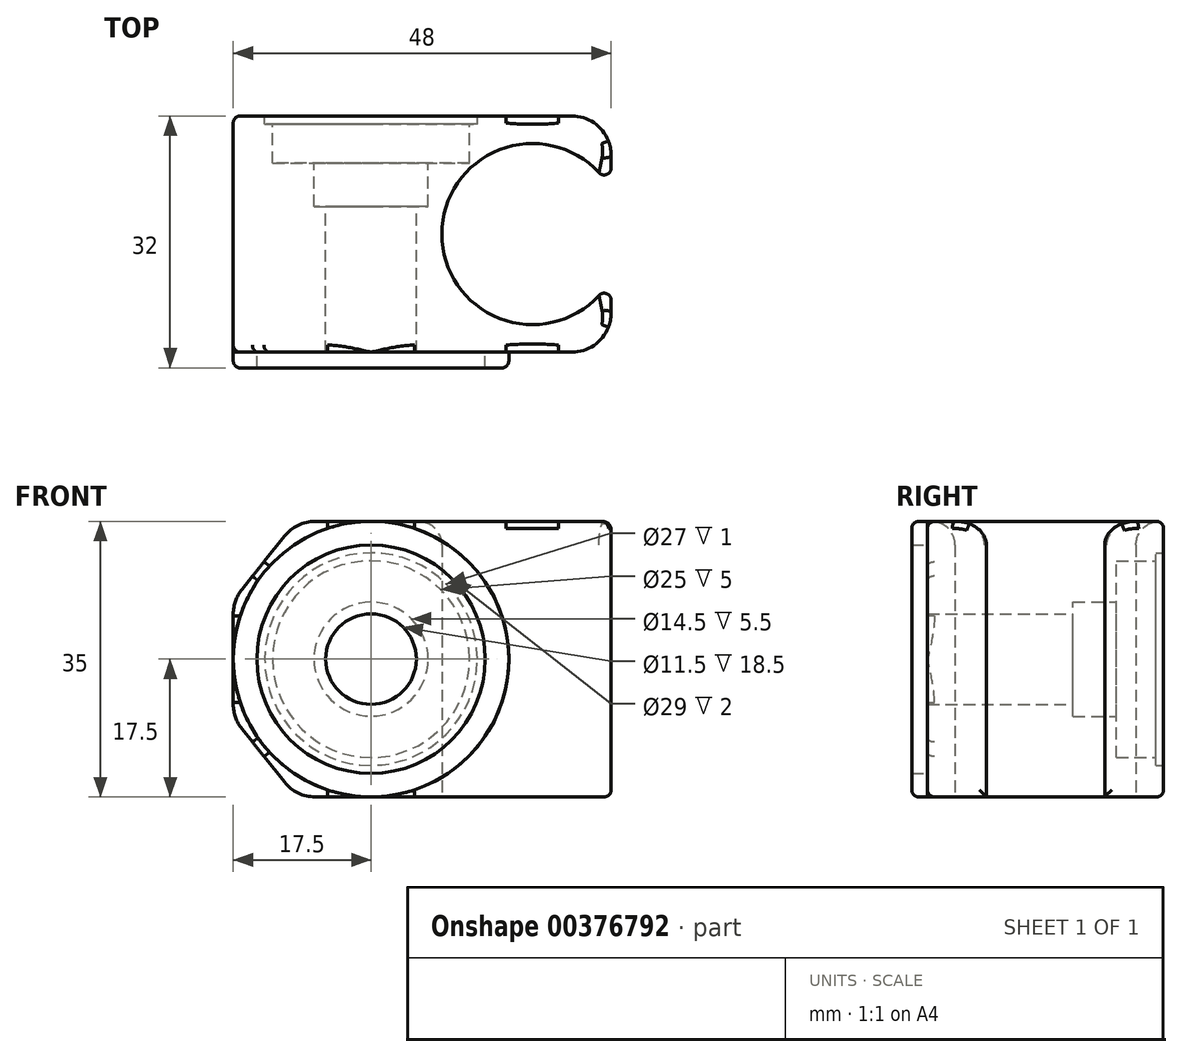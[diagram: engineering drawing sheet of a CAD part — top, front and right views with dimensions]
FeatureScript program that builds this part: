
annotation { "Feature Type Name" : "Feature", "Feature Type Description" : "" }
export const myFeature = defineFeature(function(context is Context, id is Id, definition is map)
    precondition{}
    {
        {
            var Q0;
            Q0=qCreatedBy(makeId("Front.planeOp"),FACE);
            var sketch = newSketch(context, id + "F0", { "sketchPlane" : qUnion([Q0])});
            skLineSegment(sketch, "E0.bottom", {"start": v(0, 0) * mm, "end": v(48, 0) * mm});
            skLineSegment(sketch, "E0.top", {"start": v(0, 35) * mm, "end": v(48, 35) * mm});
            skLineSegment(sketch, "E0.left", {"start": v(0, 0) * mm, "end": v(0, 35) * mm});
            skLineSegment(sketch, "E0.right", {"start": v(48, 0) * mm, "end": v(48, 35) * mm});
            skLineSegment(sketch, "E1", {"start": v(0, 17.5) * mm, "end": v(48, 17.5) * mm, "construction": true});
            skCircle(sketch, "E2", {"center": v(17.5, 17.5) * mm, "radius": 12.5 * mm});
            skCircle(sketch, "E3", {"center": v(17.5, 17.5) * mm, "radius": 7.25 * mm});
            skCircle(sketch, "E4", {"center": v(17.5, 17.5) * mm, "radius": 5.75 * mm});
            skCircle(sketch, "E5", {"center": v(17.5, 17.5) * mm, "radius": 13.5 * mm});
            skCircle(sketch, "E6", {"center": v(17.5, 17.5) * mm, "radius": 17.5 * mm});
            skCircle(sketch, "E7", {"center": v(17.5, 17.5) * mm, "radius": 14.5 * mm});
            skSolve(sketch);
        }
        {
            var Q0;
            {var subQ0=sQuery(id+"F0.wireOp",EDGE,"E0.left");var subQ1=sQuery(id+"F0.wireOp",EDGE,"E0.top");var subQ2=makeQuery(id+"F0.imprint","INTERSECT",VERTEX,{"derivedFrom":[subQ1,subQ0]});Q0=makeQuery(id+"F0.imprint","IMPRINT",FACE,{"disambiguationData":[TD([[makeQuery(id+"F0.imprint","IMPRINT",EDGE,{"disambiguationData":[TD([[subQ2,-1.0]])],"derivedFrom":subQ1}),-1.0]])]});}
            var Q1;
            {var subQ0=sQuery(id+"F0.wireOp",EDGE,"E0.right");Q1=makeQuery(id+"F0.imprint","IMPRINT",FACE,{"disambiguationData":[TD([[makeQuery(id+"F0.imprint","IMPRINT",EDGE,{"derivedFrom":subQ0}),1.0]])]});}
            var Q2;
            {var subQ0=sQuery(id+"F0.wireOp",EDGE,"E0.left");var subQ1=sQuery(id+"F0.wireOp",EDGE,"E0.bottom");var subQ2=makeQuery(id+"F0.imprint","INTERSECT",VERTEX,{"derivedFrom":[subQ1,subQ0]});Q2=makeQuery(id+"F0.imprint","IMPRINT",FACE,{"disambiguationData":[TD([[makeQuery(id+"F0.imprint","IMPRINT",EDGE,{"disambiguationData":[TD([[subQ2,-1.0]])],"derivedFrom":subQ1}),1.0]])]});}
            var Q3;
            Q3=makeQuery(id+"F0.imprint","IMPRINT",FACE,{"disambiguationData":[TD([[makeQuery(id+"F0.imprint","IMPRINT",EDGE,{"derivedFrom":sQuery(id+"F0.wireOp",EDGE,"E7")}),-1.0]])]});
            var Q4;
            Q4=makeQuery(id+"F0.imprint","IMPRINT",FACE,{"disambiguationData":[TD([[makeQuery(id+"F0.imprint","IMPRINT",EDGE,{"derivedFrom":sQuery(id+"F0.wireOp",EDGE,"E5")}),-1.0]])]});
            var Q5;
            Q5=makeQuery(id+"F0.imprint","IMPRINT",FACE,{"disambiguationData":[TD([[makeQuery(id+"F0.imprint","IMPRINT",EDGE,{"derivedFrom":sQuery(id+"F0.wireOp",EDGE,"E2")}),-1.0]])]});
            var Q6;
            Q6=makeQuery(id+"F0.imprint","IMPRINT",FACE,{"disambiguationData":[TD([[makeQuery(id+"F0.imprint","IMPRINT",EDGE,{"derivedFrom":sQuery(id+"F0.wireOp",EDGE,"E2")}),1.0]])]});
            var Q7;
            Q7=makeQuery(id+"F0.imprint","IMPRINT",FACE,{"disambiguationData":[TD([[makeQuery(id+"F0.imprint","IMPRINT",EDGE,{"derivedFrom":sQuery(id+"F0.wireOp",EDGE,"E3")}),1.0]])]});
            var Q8;
            Q8=makeQuery(id+"F0.imprint","IMPRINT",FACE,{"disambiguationData":[TD([[makeQuery(id+"F0.imprint","IMPRINT",EDGE,{"derivedFrom":sQuery(id+"F0.wireOp",EDGE,"E4")}),1.0]])]});
            extrude(context, id + "F1", {"entities" : qUnion([Q0, Q1, Q2, Q3, Q4, Q5, Q6, Q7, Q8]), "depth" : 30 * mm});
        }
        {
            var Q0;
            Q0=makeQuery(id+"F0.imprint","IMPRINT",FACE,{"disambiguationData":[TD([[makeQuery(id+"F0.imprint","IMPRINT",EDGE,{"derivedFrom":sQuery(id+"F0.wireOp",EDGE,"E2")}),-1.0]])]});
            var Q1;
            Q1=makeQuery(id+"F0.imprint","IMPRINT",FACE,{"disambiguationData":[TD([[makeQuery(id+"F0.imprint","IMPRINT",EDGE,{"derivedFrom":sQuery(id+"F0.wireOp",EDGE,"E2")}),1.0]])]});
            var Q2;
            Q2=makeQuery(id+"F0.imprint","IMPRINT",FACE,{"disambiguationData":[TD([[makeQuery(id+"F0.imprint","IMPRINT",EDGE,{"derivedFrom":sQuery(id+"F0.wireOp",EDGE,"E3")}),1.0]])]});
            var Q3;
            Q3=makeQuery(id+"F0.imprint","IMPRINT",FACE,{"disambiguationData":[TD([[makeQuery(id+"F0.imprint","IMPRINT",EDGE,{"derivedFrom":sQuery(id+"F0.wireOp",EDGE,"E4")}),1.0]])]});
            extrude(context, id + "F2", {"entities" : qUnion([Q0, Q1, Q2, Q3]), "operationType" : NewBodyOperationType.REMOVE, "depth" : 1 * mm});
        }
        {
            var Q0;
            Q0=makeQuery(id+"F0.imprint","IMPRINT",FACE,{"disambiguationData":[TD([[makeQuery(id+"F0.imprint","IMPRINT",EDGE,{"derivedFrom":sQuery(id+"F0.wireOp",EDGE,"E2")}),1.0]])]});
            var Q1;
            Q1=makeQuery(id+"F0.imprint","IMPRINT",FACE,{"disambiguationData":[TD([[makeQuery(id+"F0.imprint","IMPRINT",EDGE,{"derivedFrom":sQuery(id+"F0.wireOp",EDGE,"E4")}),1.0]])]});
            var Q2;
            Q2=makeQuery(id+"F0.imprint","IMPRINT",FACE,{"disambiguationData":[TD([[makeQuery(id+"F0.imprint","IMPRINT",EDGE,{"derivedFrom":sQuery(id+"F0.wireOp",EDGE,"E3")}),1.0]])]});
            extrude(context, id + "F3", {"entities" : qUnion([Q0, Q1, Q2]), "operationType" : NewBodyOperationType.REMOVE, "depth" : 6 * mm});
        }
        {
            var Q0;
            Q0=makeQuery(id+"F0.imprint","IMPRINT",FACE,{"disambiguationData":[TD([[makeQuery(id+"F0.imprint","IMPRINT",EDGE,{"derivedFrom":sQuery(id+"F0.wireOp",EDGE,"E3")}),1.0]])]});
            var Q1;
            Q1=makeQuery(id+"F0.imprint","IMPRINT",FACE,{"disambiguationData":[TD([[makeQuery(id+"F0.imprint","IMPRINT",EDGE,{"derivedFrom":sQuery(id+"F0.wireOp",EDGE,"E4")}),1.0]])]});
            extrude(context, id + "F4", {"entities" : qUnion([Q0, Q1]), "operationType" : NewBodyOperationType.REMOVE, "depth" : 11.5 * mm});
        }
        {
            var Q0;
            Q0=makeQuery(id+"F0.imprint","IMPRINT",FACE,{"disambiguationData":[TD([[makeQuery(id+"F0.imprint","IMPRINT",EDGE,{"derivedFrom":sQuery(id+"F0.wireOp",EDGE,"E4")}),1.0]])]});
            extrude(context, id + "F5", {"entities" : qUnion([Q0]), "operationType" : NewBodyOperationType.REMOVE, "endBound" : BoundingType.THROUGH_ALL, "depth" : 25 * mm});
        }
        {
            var Q0;
            Q0=makeQuery(id+"F0.imprint","IMPRINT",FACE,{"disambiguationData":[TD([[makeQuery(id+"F0.imprint","IMPRINT",EDGE,{"derivedFrom":sQuery(id+"F0.wireOp",EDGE,"E7")}),-1.0]])]});
            extrude(context, id + "F6", {"entities" : qUnion([Q0]), "operationType" : NewBodyOperationType.ADD, "depth" : 32 * mm});
        }
        {
            var Q0;
            Q0=qCreatedBy(makeId("Top.planeOp"),FACE);
            var sketch = newSketch(context, id + "F7", { "sketchPlane" : qUnion([Q0])});
            skCircle(sketch, "E8", {"center": v(38, -15) * mm, "radius": 11.5 * mm});
            skLineSegment(sketch, "E9", {"start": v(48, -15) * mm, "end": v(0, -15) * mm, "construction": true});
            skSolve(sketch);
        }
        {
            var Q0;
            Q0=makeQuery(id+"F7.imprint","IMPRINT",FACE,{"disambiguationData":[TD([[makeQuery(id+"F7.imprint","IMPRINT",EDGE,{"derivedFrom":sQuery(id+"F7.wireOp",EDGE,"E8")}),1.0]])]});
            extrude(context, id + "F8", {"entities" : qUnion([Q0]), "operationType" : NewBodyOperationType.REMOVE, "endBound" : BoundingType.THROUGH_ALL, "depth" : 25 * mm});
        }
        {
            var Q0;
            Q0=makeQuery(id+"F1.opExtrude","SWEPT_EDGE",EDGE,{"disambiguationData":[OSD([sQuery(id+"F0.wireOp",EDGE,"E0.bottom"),sQuery(id+"F0.wireOp",EDGE,"E0.left")])]});
            var Q1;
            Q1=makeQuery(id+"F1.opExtrude","SWEPT_EDGE",EDGE,{"disambiguationData":[OSD([sQuery(id+"F0.wireOp",EDGE,"E0.top"),sQuery(id+"F0.wireOp",EDGE,"E0.left")])]});
            chamfer(context, id + "F9", {"entities" : qUnion([Q0, Q1]), "chamferType" : ChamferType.TWO_OFFSETS, "width1" : 8 * mm, "oppositeDirection" : false, "width2" : 10 * mm, "tangentPropagation" : true});
        }
        {
            var Q0;
            {var subQ0=sQuery(id+"F0.wireOp",EDGE,"E0.left");Q0=makeQuery(id+"F9.opChamfer","BLEND_EDGE",EDGE,{"blendedFrom":[makeQuery(id+"F1.opExtrude","SWEPT_EDGE",EDGE,{"disambiguationData":[OSD([sQuery(id+"F0.wireOp",EDGE,"E0.bottom"),subQ0])]}),makeQuery(id+"F1.opExtrude","SWEPT_FACE",FACE,{"disambiguationData":[OSD([subQ0])]})],"blendedInto":[makeQuery(id+"F1.opExtrude","SWEPT_FACE",FACE,{"disambiguationData":[OSD([subQ0])]})]});}
            var Q1;
            {var subQ0=sQuery(id+"F0.wireOp",EDGE,"E0.left");Q1=makeQuery(id+"F9.opChamfer","BLEND_EDGE",EDGE,{"blendedFrom":[makeQuery(id+"F1.opExtrude","SWEPT_EDGE",EDGE,{"disambiguationData":[OSD([sQuery(id+"F0.wireOp",EDGE,"E0.top"),subQ0])]}),makeQuery(id+"F1.opExtrude","SWEPT_FACE",FACE,{"disambiguationData":[OSD([subQ0])]})],"blendedInto":[makeQuery(id+"F1.opExtrude","SWEPT_FACE",FACE,{"disambiguationData":[OSD([subQ0])]})]});}
            var Q2;
            {var subQ0=sQuery(id+"F0.wireOp",EDGE,"E0.top");Q2=makeQuery(id+"F9.opChamfer","BLEND_EDGE",EDGE,{"blendedFrom":[makeQuery(id+"F1.opExtrude","SWEPT_EDGE",EDGE,{"disambiguationData":[OSD([subQ0,sQuery(id+"F0.wireOp",EDGE,"E0.left")])]}),makeQuery(id+"F1.opExtrude","SWEPT_FACE",FACE,{"disambiguationData":[OSD([subQ0])]})],"blendedInto":[makeQuery(id+"F1.opExtrude","SWEPT_FACE",FACE,{"disambiguationData":[OSD([subQ0])]})]});}
            var Q3;
            {var subQ0=sQuery(id+"F0.wireOp",EDGE,"E0.bottom");Q3=makeQuery(id+"F9.opChamfer","BLEND_EDGE",EDGE,{"blendedFrom":[makeQuery(id+"F1.opExtrude","SWEPT_EDGE",EDGE,{"disambiguationData":[OSD([subQ0,sQuery(id+"F0.wireOp",EDGE,"E0.left")])]}),makeQuery(id+"F1.opExtrude","SWEPT_FACE",FACE,{"disambiguationData":[OSD([subQ0])]})],"blendedInto":[makeQuery(id+"F1.opExtrude","SWEPT_FACE",FACE,{"disambiguationData":[OSD([subQ0])]})]});}
            var Q4;
            Q4=makeQuery(id+"F1.opExtrude","CAP_EDGE",EDGE,{"disambiguationData":[OSD([sQuery(id+"F0.wireOp",EDGE,"E0.right")])],"isStart":false});
            var Q5;
            Q5=makeQuery(id+"F1.opExtrude","CAP_EDGE",EDGE,{"disambiguationData":[OSD([sQuery(id+"F0.wireOp",EDGE,"E0.right")])],"isStart":true});
            fillet(context, id + "F10", {"entities" : qUnion([Q0, Q1, Q2, Q3, Q4, Q5]), "radius" : 5 * mm, "tangentPropagation" : true, "allowEdgeOverflow" : false});
        }
        {
            var Q0;
            Q0=makeQuery(id+"F8.boolean.opBoolean","INTERSECT",EDGE,{"derivedFrom":[makeQuery(id+"F1.opExtrude","SWEPT_FACE",FACE,{"disambiguationData":[OSD([sQuery(id+"F0.wireOp",EDGE,"E0.top")])]}),makeQuery(id+"F8.opExtrude","SWEPT_FACE",FACE,{"disambiguationData":[OSD([sQuery(id+"F7.wireOp",EDGE,"E8")])]})]});
            var Q1;
            Q1=makeQuery(id+"F8.boolean.opBoolean","COPY",EDGE,{"derivedFrom":makeQuery(id+"F8.opExtrude","CAP_EDGE",EDGE,{"disambiguationData":[OSD([sQuery(id+"F7.wireOp",EDGE,"E8")])],"isStart":true})});
            fillet(context, id + "F11", {"entities" : qUnion([Q0, Q1]), "radius" : 3 * mm, "tangentPropagation" : true, "allowEdgeOverflow" : false});
        }
        {
            var Q0;
            {var subQ0=sQuery(id+"F0.wireOp",EDGE,"E0.bottom");var subQ1=sQuery(id+"F0.wireOp",EDGE,"E0.right");Q0=makeQuery(id+"F6.boolean.opBoolean","SPLIT",EDGE,{"disambiguationData":[TD([makeQuery(id+"F1.opExtrude","SWEPT_FACE",FACE,{"disambiguationData":[OSD([subQ1])]})])],"derivedFrom":makeQuery(id+"F1.opExtrude","CAP_EDGE",EDGE,{"disambiguationData":[OSD([subQ0])],"isStart":false})});}
            var Q1;
            Q1=makeQuery(id+"F10.opFillet","BLEND_EDGE",EDGE,{"blendedFrom":[makeQuery(id+"F1.opExtrude","CAP_EDGE",EDGE,{"disambiguationData":[OSD([sQuery(id+"F0.wireOp",EDGE,"E0.right")])],"isStart":false}),makeQuery(id+"F1.opExtrude","SWEPT_FACE",FACE,{"disambiguationData":[OSD([sQuery(id+"F0.wireOp",EDGE,"E0.bottom")])]})],"blendedInto":[makeQuery(id+"F1.opExtrude","SWEPT_FACE",FACE,{"disambiguationData":[OSD([sQuery(id+"F0.wireOp",EDGE,"E0.bottom")])]})]});
            var Q2;
            {var subQ0=sQuery(id+"F0.wireOp",EDGE,"E0.bottom");var subQ1=sQuery(id+"F0.wireOp",EDGE,"E0.left");Q2=makeQuery(id+"F6.boolean.opBoolean","SPLIT",EDGE,{"disambiguationData":[TD([makeQuery(id+"F1.opExtrude","SWEPT_FACE",FACE,{"disambiguationData":[OSD([subQ1])]})])],"derivedFrom":makeQuery(id+"F1.opExtrude","CAP_EDGE",EDGE,{"disambiguationData":[OSD([subQ0])],"isStart":false})});}
            var Q3;
            {var subQ0=sQuery(id+"F0.wireOp",EDGE,"E0.bottom");var subQ1=makeQuery(id+"F1.opExtrude","SWEPT_FACE",FACE,{"disambiguationData":[OSD([subQ0])]});var subQ2=sQuery(id+"F0.wireOp",EDGE,"E0.left");var subQ3=makeQuery(id+"F1.opExtrude","CAP_FACE",FACE,{"disambiguationData":[OSD([subQ0,sQuery(id+"F0.wireOp",EDGE,"E0.top"),subQ2,sQuery(id+"F0.wireOp",EDGE,"E0.right")])],"isStart":false});Q3=makeQuery(id+"F10.opFillet","BLEND_EDGE",EDGE,{"blendedFrom":[makeQuery(id+"F9.opChamfer","BLEND_EDGE",EDGE,{"blendedFrom":[makeQuery(id+"F1.opExtrude","SWEPT_EDGE",EDGE,{"disambiguationData":[OSD([subQ0,subQ2])]}),subQ1],"blendedInto":[subQ1]}),makeQuery(id+"F6.boolean.opBoolean","SPLIT",FACE,{"disambiguationData":[TD([subQ1,subQ3,makeQuery(id+"F1.opExtrude","SWEPT_FACE",FACE,{"disambiguationData":[OSD([subQ2])]}),makeQuery(id+"F6.opExtrude","SWEPT_FACE",FACE,{"disambiguationData":[OSD([sQuery(id+"F0.wireOp",EDGE,"E6")])]})])],"derivedFrom":subQ3})],"blendedInto":[makeQuery(id+"F6.boolean.opBoolean","SPLIT",FACE,{"disambiguationData":[TD([subQ1,subQ3,makeQuery(id+"F1.opExtrude","SWEPT_FACE",FACE,{"disambiguationData":[OSD([subQ2])]}),makeQuery(id+"F6.opExtrude","SWEPT_FACE",FACE,{"disambiguationData":[OSD([sQuery(id+"F0.wireOp",EDGE,"E6")])]})])],"derivedFrom":subQ3})]});}
            var Q4;
            {var subQ0=sQuery(id+"F0.wireOp",EDGE,"E0.bottom");var subQ1=sQuery(id+"F0.wireOp",EDGE,"E0.left");var subQ2=makeQuery(id+"F1.opExtrude","CAP_FACE",FACE,{"disambiguationData":[OSD([subQ0,sQuery(id+"F0.wireOp",EDGE,"E0.top"),subQ1,sQuery(id+"F0.wireOp",EDGE,"E0.right")])],"isStart":false});Q4=makeQuery(id+"F9.opChamfer","BLEND_EDGE",EDGE,{"blendedFrom":[makeQuery(id+"F1.opExtrude","SWEPT_EDGE",EDGE,{"disambiguationData":[OSD([subQ0,subQ1])]}),makeQuery(id+"F6.boolean.opBoolean","SPLIT",FACE,{"disambiguationData":[TD([makeQuery(id+"F1.opExtrude","SWEPT_FACE",FACE,{"disambiguationData":[OSD([subQ0])]}),subQ2,makeQuery(id+"F1.opExtrude","SWEPT_FACE",FACE,{"disambiguationData":[OSD([subQ1])]}),makeQuery(id+"F6.opExtrude","SWEPT_FACE",FACE,{"disambiguationData":[OSD([sQuery(id+"F0.wireOp",EDGE,"E6")])]})])],"derivedFrom":subQ2})],"blendedInto":[makeQuery(id+"F6.boolean.opBoolean","SPLIT",FACE,{"disambiguationData":[TD([makeQuery(id+"F1.opExtrude","SWEPT_FACE",FACE,{"disambiguationData":[OSD([subQ0])]}),subQ2,makeQuery(id+"F1.opExtrude","SWEPT_FACE",FACE,{"disambiguationData":[OSD([subQ1])]}),makeQuery(id+"F6.opExtrude","SWEPT_FACE",FACE,{"disambiguationData":[OSD([sQuery(id+"F0.wireOp",EDGE,"E6")])]})])],"derivedFrom":subQ2})]});}
            var Q5;
            {var subQ0=sQuery(id+"F0.wireOp",EDGE,"E0.bottom");var subQ1=sQuery(id+"F0.wireOp",EDGE,"E0.left");var subQ2=makeQuery(id+"F1.opExtrude","CAP_FACE",FACE,{"disambiguationData":[OSD([subQ0,sQuery(id+"F0.wireOp",EDGE,"E0.top"),subQ1,sQuery(id+"F0.wireOp",EDGE,"E0.right")])],"isStart":false});var subQ3=makeQuery(id+"F1.opExtrude","SWEPT_FACE",FACE,{"disambiguationData":[OSD([subQ1])]});Q5=makeQuery(id+"F10.opFillet","BLEND_EDGE",EDGE,{"blendedFrom":[makeQuery(id+"F9.opChamfer","BLEND_EDGE",EDGE,{"blendedFrom":[makeQuery(id+"F1.opExtrude","SWEPT_EDGE",EDGE,{"disambiguationData":[OSD([subQ0,subQ1])]}),subQ3],"blendedInto":[subQ3]}),makeQuery(id+"F6.boolean.opBoolean","SPLIT",FACE,{"disambiguationData":[TD([makeQuery(id+"F1.opExtrude","SWEPT_FACE",FACE,{"disambiguationData":[OSD([subQ0])]}),subQ2,subQ3,makeQuery(id+"F6.opExtrude","SWEPT_FACE",FACE,{"disambiguationData":[OSD([sQuery(id+"F0.wireOp",EDGE,"E6")])]})])],"derivedFrom":subQ2})],"blendedInto":[makeQuery(id+"F6.boolean.opBoolean","SPLIT",FACE,{"disambiguationData":[TD([makeQuery(id+"F1.opExtrude","SWEPT_FACE",FACE,{"disambiguationData":[OSD([subQ0])]}),subQ2,subQ3,makeQuery(id+"F6.opExtrude","SWEPT_FACE",FACE,{"disambiguationData":[OSD([sQuery(id+"F0.wireOp",EDGE,"E6")])]})])],"derivedFrom":subQ2})]});}
            var Q6;
            {var subQ0=sQuery(id+"F0.wireOp",EDGE,"E0.bottom");var subQ1=sQuery(id+"F0.wireOp",EDGE,"E0.left");Q6=makeQuery(id+"F6.boolean.opBoolean","SPLIT",EDGE,{"disambiguationData":[TD([makeQuery(id+"F1.opExtrude","SWEPT_FACE",FACE,{"disambiguationData":[OSD([subQ0])]})])],"derivedFrom":makeQuery(id+"F1.opExtrude","CAP_EDGE",EDGE,{"disambiguationData":[OSD([subQ1])],"isStart":false})});}
            var Q7;
            {var subQ0=sQuery(id+"F0.wireOp",EDGE,"E0.left");var subQ1=sQuery(id+"F0.wireOp",EDGE,"E0.top");Q7=makeQuery(id+"F6.boolean.opBoolean","SPLIT",EDGE,{"disambiguationData":[TD([makeQuery(id+"F1.opExtrude","SWEPT_FACE",FACE,{"disambiguationData":[OSD([subQ1])]})])],"derivedFrom":makeQuery(id+"F1.opExtrude","CAP_EDGE",EDGE,{"disambiguationData":[OSD([subQ0])],"isStart":false})});}
            var Q8;
            {var subQ0=sQuery(id+"F0.wireOp",EDGE,"E0.left");var subQ1=sQuery(id+"F0.wireOp",EDGE,"E0.top");var subQ2=makeQuery(id+"F1.opExtrude","CAP_FACE",FACE,{"disambiguationData":[OSD([sQuery(id+"F0.wireOp",EDGE,"E0.bottom"),subQ1,subQ0,sQuery(id+"F0.wireOp",EDGE,"E0.right")])],"isStart":false});var subQ3=makeQuery(id+"F1.opExtrude","SWEPT_FACE",FACE,{"disambiguationData":[OSD([subQ0])]});Q8=makeQuery(id+"F10.opFillet","BLEND_EDGE",EDGE,{"blendedFrom":[makeQuery(id+"F9.opChamfer","BLEND_EDGE",EDGE,{"blendedFrom":[makeQuery(id+"F1.opExtrude","SWEPT_EDGE",EDGE,{"disambiguationData":[OSD([subQ1,subQ0])]}),subQ3],"blendedInto":[subQ3]}),makeQuery(id+"F6.boolean.opBoolean","SPLIT",FACE,{"disambiguationData":[TD([subQ2,makeQuery(id+"F1.opExtrude","SWEPT_FACE",FACE,{"disambiguationData":[OSD([subQ1])]}),subQ3,makeQuery(id+"F6.opExtrude","SWEPT_FACE",FACE,{"disambiguationData":[OSD([sQuery(id+"F0.wireOp",EDGE,"E6")])]})])],"derivedFrom":subQ2})],"blendedInto":[makeQuery(id+"F6.boolean.opBoolean","SPLIT",FACE,{"disambiguationData":[TD([subQ2,makeQuery(id+"F1.opExtrude","SWEPT_FACE",FACE,{"disambiguationData":[OSD([subQ1])]}),subQ3,makeQuery(id+"F6.opExtrude","SWEPT_FACE",FACE,{"disambiguationData":[OSD([sQuery(id+"F0.wireOp",EDGE,"E6")])]})])],"derivedFrom":subQ2})]});}
            var Q9;
            {var subQ0=sQuery(id+"F0.wireOp",EDGE,"E0.left");var subQ1=sQuery(id+"F0.wireOp",EDGE,"E0.top");var subQ2=makeQuery(id+"F1.opExtrude","CAP_FACE",FACE,{"disambiguationData":[OSD([sQuery(id+"F0.wireOp",EDGE,"E0.bottom"),subQ1,subQ0,sQuery(id+"F0.wireOp",EDGE,"E0.right")])],"isStart":false});Q9=makeQuery(id+"F9.opChamfer","BLEND_EDGE",EDGE,{"blendedFrom":[makeQuery(id+"F1.opExtrude","SWEPT_EDGE",EDGE,{"disambiguationData":[OSD([subQ1,subQ0])]}),makeQuery(id+"F6.boolean.opBoolean","SPLIT",FACE,{"disambiguationData":[TD([subQ2,makeQuery(id+"F1.opExtrude","SWEPT_FACE",FACE,{"disambiguationData":[OSD([subQ1])]}),makeQuery(id+"F1.opExtrude","SWEPT_FACE",FACE,{"disambiguationData":[OSD([subQ0])]}),makeQuery(id+"F6.opExtrude","SWEPT_FACE",FACE,{"disambiguationData":[OSD([sQuery(id+"F0.wireOp",EDGE,"E6")])]})])],"derivedFrom":subQ2})],"blendedInto":[makeQuery(id+"F6.boolean.opBoolean","SPLIT",FACE,{"disambiguationData":[TD([subQ2,makeQuery(id+"F1.opExtrude","SWEPT_FACE",FACE,{"disambiguationData":[OSD([subQ1])]}),makeQuery(id+"F1.opExtrude","SWEPT_FACE",FACE,{"disambiguationData":[OSD([subQ0])]}),makeQuery(id+"F6.opExtrude","SWEPT_FACE",FACE,{"disambiguationData":[OSD([sQuery(id+"F0.wireOp",EDGE,"E6")])]})])],"derivedFrom":subQ2})]});}
            var Q10;
            {var subQ0=sQuery(id+"F0.wireOp",EDGE,"E0.left");var subQ1=sQuery(id+"F0.wireOp",EDGE,"E0.top");Q10=makeQuery(id+"F6.boolean.opBoolean","SPLIT",EDGE,{"disambiguationData":[TD([makeQuery(id+"F1.opExtrude","SWEPT_FACE",FACE,{"disambiguationData":[OSD([subQ0])]})])],"derivedFrom":makeQuery(id+"F1.opExtrude","CAP_EDGE",EDGE,{"disambiguationData":[OSD([subQ1])],"isStart":false})});}
            var Q11;
            {var subQ0=sQuery(id+"F0.wireOp",EDGE,"E0.right");var subQ1=sQuery(id+"F0.wireOp",EDGE,"E0.top");Q11=makeQuery(id+"F6.boolean.opBoolean","SPLIT",EDGE,{"disambiguationData":[TD([makeQuery(id+"F1.opExtrude","SWEPT_FACE",FACE,{"disambiguationData":[OSD([subQ0])]})])],"derivedFrom":makeQuery(id+"F1.opExtrude","CAP_EDGE",EDGE,{"disambiguationData":[OSD([subQ1])],"isStart":false})});}
            var Q12;
            Q12=makeQuery(id+"F10.opFillet","BLEND_EDGE",EDGE,{"blendedFrom":[makeQuery(id+"F1.opExtrude","CAP_EDGE",EDGE,{"disambiguationData":[OSD([sQuery(id+"F0.wireOp",EDGE,"E0.right")])],"isStart":false}),makeQuery(id+"F1.opExtrude","SWEPT_FACE",FACE,{"disambiguationData":[OSD([sQuery(id+"F0.wireOp",EDGE,"E0.top")])]})],"blendedInto":[makeQuery(id+"F1.opExtrude","SWEPT_FACE",FACE,{"disambiguationData":[OSD([sQuery(id+"F0.wireOp",EDGE,"E0.top")])]})]});
            var Q13;
            Q13=makeQuery(id+"F1.opExtrude","CAP_EDGE",EDGE,{"disambiguationData":[OSD([sQuery(id+"F0.wireOp",EDGE,"E0.top")])],"isStart":true});
            var Q14;
            Q14=makeQuery(id+"F10.opFillet","BLEND_EDGE",EDGE,{"blendedFrom":[makeQuery(id+"F1.opExtrude","CAP_EDGE",EDGE,{"disambiguationData":[OSD([sQuery(id+"F0.wireOp",EDGE,"E0.right")])],"isStart":true}),makeQuery(id+"F1.opExtrude","SWEPT_FACE",FACE,{"disambiguationData":[OSD([sQuery(id+"F0.wireOp",EDGE,"E0.top")])]})],"blendedInto":[makeQuery(id+"F1.opExtrude","SWEPT_FACE",FACE,{"disambiguationData":[OSD([sQuery(id+"F0.wireOp",EDGE,"E0.top")])]})]});
            var Q15;
            {var subQ0=sQuery(id+"F0.wireOp",EDGE,"E0.left");var subQ1=sQuery(id+"F0.wireOp",EDGE,"E0.top");Q15=makeQuery(id+"F10.opFillet","BLEND_EDGE",EDGE,{"blendedFrom":[makeQuery(id+"F9.opChamfer","BLEND_EDGE",EDGE,{"blendedFrom":[makeQuery(id+"F1.opExtrude","SWEPT_EDGE",EDGE,{"disambiguationData":[OSD([subQ1,subQ0])]}),makeQuery(id+"F1.opExtrude","SWEPT_FACE",FACE,{"disambiguationData":[OSD([subQ1])]})],"blendedInto":[makeQuery(id+"F1.opExtrude","SWEPT_FACE",FACE,{"disambiguationData":[OSD([subQ1])]})]}),makeQuery(id+"F1.opExtrude","CAP_FACE",FACE,{"disambiguationData":[OSD([sQuery(id+"F0.wireOp",EDGE,"E0.bottom"),subQ1,subQ0,sQuery(id+"F0.wireOp",EDGE,"E0.right")])],"isStart":true})],"blendedInto":[makeQuery(id+"F1.opExtrude","CAP_FACE",FACE,{"disambiguationData":[OSD([sQuery(id+"F0.wireOp",EDGE,"E0.bottom"),subQ1,subQ0,sQuery(id+"F0.wireOp",EDGE,"E0.right")])],"isStart":true})]});}
            var Q16;
            {var subQ0=sQuery(id+"F0.wireOp",EDGE,"E0.left");var subQ1=sQuery(id+"F0.wireOp",EDGE,"E0.top");Q16=makeQuery(id+"F9.opChamfer","BLEND_EDGE",EDGE,{"blendedFrom":[makeQuery(id+"F1.opExtrude","SWEPT_EDGE",EDGE,{"disambiguationData":[OSD([subQ1,subQ0])]}),makeQuery(id+"F1.opExtrude","CAP_FACE",FACE,{"disambiguationData":[OSD([sQuery(id+"F0.wireOp",EDGE,"E0.bottom"),subQ1,subQ0,sQuery(id+"F0.wireOp",EDGE,"E0.right")])],"isStart":true})],"blendedInto":[makeQuery(id+"F1.opExtrude","CAP_FACE",FACE,{"disambiguationData":[OSD([sQuery(id+"F0.wireOp",EDGE,"E0.bottom"),subQ1,subQ0,sQuery(id+"F0.wireOp",EDGE,"E0.right")])],"isStart":true})]});}
            var Q17;
            {var subQ0=sQuery(id+"F0.wireOp",EDGE,"E0.left");var subQ1=sQuery(id+"F0.wireOp",EDGE,"E0.top");Q17=makeQuery(id+"F10.opFillet","BLEND_EDGE",EDGE,{"blendedFrom":[makeQuery(id+"F9.opChamfer","BLEND_EDGE",EDGE,{"blendedFrom":[makeQuery(id+"F1.opExtrude","SWEPT_EDGE",EDGE,{"disambiguationData":[OSD([subQ1,subQ0])]}),makeQuery(id+"F1.opExtrude","SWEPT_FACE",FACE,{"disambiguationData":[OSD([subQ0])]})],"blendedInto":[makeQuery(id+"F1.opExtrude","SWEPT_FACE",FACE,{"disambiguationData":[OSD([subQ0])]})]}),makeQuery(id+"F1.opExtrude","CAP_FACE",FACE,{"disambiguationData":[OSD([sQuery(id+"F0.wireOp",EDGE,"E0.bottom"),subQ1,subQ0,sQuery(id+"F0.wireOp",EDGE,"E0.right")])],"isStart":true})],"blendedInto":[makeQuery(id+"F1.opExtrude","CAP_FACE",FACE,{"disambiguationData":[OSD([sQuery(id+"F0.wireOp",EDGE,"E0.bottom"),subQ1,subQ0,sQuery(id+"F0.wireOp",EDGE,"E0.right")])],"isStart":true})]});}
            var Q18;
            Q18=makeQuery(id+"F1.opExtrude","CAP_EDGE",EDGE,{"disambiguationData":[OSD([sQuery(id+"F0.wireOp",EDGE,"E0.left")])],"isStart":true});
            var Q19;
            {var subQ0=sQuery(id+"F0.wireOp",EDGE,"E0.left");var subQ1=sQuery(id+"F0.wireOp",EDGE,"E0.bottom");Q19=makeQuery(id+"F10.opFillet","BLEND_EDGE",EDGE,{"blendedFrom":[makeQuery(id+"F9.opChamfer","BLEND_EDGE",EDGE,{"blendedFrom":[makeQuery(id+"F1.opExtrude","SWEPT_EDGE",EDGE,{"disambiguationData":[OSD([subQ1,subQ0])]}),makeQuery(id+"F1.opExtrude","SWEPT_FACE",FACE,{"disambiguationData":[OSD([subQ0])]})],"blendedInto":[makeQuery(id+"F1.opExtrude","SWEPT_FACE",FACE,{"disambiguationData":[OSD([subQ0])]})]}),makeQuery(id+"F1.opExtrude","CAP_FACE",FACE,{"disambiguationData":[OSD([subQ1,sQuery(id+"F0.wireOp",EDGE,"E0.top"),subQ0,sQuery(id+"F0.wireOp",EDGE,"E0.right")])],"isStart":true})],"blendedInto":[makeQuery(id+"F1.opExtrude","CAP_FACE",FACE,{"disambiguationData":[OSD([subQ1,sQuery(id+"F0.wireOp",EDGE,"E0.top"),subQ0,sQuery(id+"F0.wireOp",EDGE,"E0.right")])],"isStart":true})]});}
            var Q20;
            {var subQ0=sQuery(id+"F0.wireOp",EDGE,"E0.left");var subQ1=sQuery(id+"F0.wireOp",EDGE,"E0.bottom");Q20=makeQuery(id+"F9.opChamfer","BLEND_EDGE",EDGE,{"blendedFrom":[makeQuery(id+"F1.opExtrude","SWEPT_EDGE",EDGE,{"disambiguationData":[OSD([subQ1,subQ0])]}),makeQuery(id+"F1.opExtrude","CAP_FACE",FACE,{"disambiguationData":[OSD([subQ1,sQuery(id+"F0.wireOp",EDGE,"E0.top"),subQ0,sQuery(id+"F0.wireOp",EDGE,"E0.right")])],"isStart":true})],"blendedInto":[makeQuery(id+"F1.opExtrude","CAP_FACE",FACE,{"disambiguationData":[OSD([subQ1,sQuery(id+"F0.wireOp",EDGE,"E0.top"),subQ0,sQuery(id+"F0.wireOp",EDGE,"E0.right")])],"isStart":true})]});}
            var Q21;
            {var subQ0=sQuery(id+"F0.wireOp",EDGE,"E0.left");var subQ1=sQuery(id+"F0.wireOp",EDGE,"E0.bottom");Q21=makeQuery(id+"F10.opFillet","BLEND_EDGE",EDGE,{"blendedFrom":[makeQuery(id+"F9.opChamfer","BLEND_EDGE",EDGE,{"blendedFrom":[makeQuery(id+"F1.opExtrude","SWEPT_EDGE",EDGE,{"disambiguationData":[OSD([subQ1,subQ0])]}),makeQuery(id+"F1.opExtrude","SWEPT_FACE",FACE,{"disambiguationData":[OSD([subQ1])]})],"blendedInto":[makeQuery(id+"F1.opExtrude","SWEPT_FACE",FACE,{"disambiguationData":[OSD([subQ1])]})]}),makeQuery(id+"F1.opExtrude","CAP_FACE",FACE,{"disambiguationData":[OSD([subQ1,sQuery(id+"F0.wireOp",EDGE,"E0.top"),subQ0,sQuery(id+"F0.wireOp",EDGE,"E0.right")])],"isStart":true})],"blendedInto":[makeQuery(id+"F1.opExtrude","CAP_FACE",FACE,{"disambiguationData":[OSD([subQ1,sQuery(id+"F0.wireOp",EDGE,"E0.top"),subQ0,sQuery(id+"F0.wireOp",EDGE,"E0.right")])],"isStart":true})]});}
            var Q22;
            Q22=makeQuery(id+"F1.opExtrude","CAP_EDGE",EDGE,{"disambiguationData":[OSD([sQuery(id+"F0.wireOp",EDGE,"E0.bottom")])],"isStart":true});
            var Q23;
            Q23=makeQuery(id+"F10.opFillet","BLEND_EDGE",EDGE,{"blendedFrom":[makeQuery(id+"F1.opExtrude","CAP_EDGE",EDGE,{"disambiguationData":[OSD([sQuery(id+"F0.wireOp",EDGE,"E0.right")])],"isStart":true}),makeQuery(id+"F1.opExtrude","SWEPT_FACE",FACE,{"disambiguationData":[OSD([sQuery(id+"F0.wireOp",EDGE,"E0.bottom")])]})],"blendedInto":[makeQuery(id+"F1.opExtrude","SWEPT_FACE",FACE,{"disambiguationData":[OSD([sQuery(id+"F0.wireOp",EDGE,"E0.bottom")])]})]});
            var Q24;
            {var subQ0=sQuery(id+"F0.wireOp",EDGE,"E0.left");var subQ1=sQuery(id+"F0.wireOp",EDGE,"E0.top");var subQ2=makeQuery(id+"F1.opExtrude","CAP_FACE",FACE,{"disambiguationData":[OSD([sQuery(id+"F0.wireOp",EDGE,"E0.bottom"),subQ1,subQ0,sQuery(id+"F0.wireOp",EDGE,"E0.right")])],"isStart":false});var subQ3=makeQuery(id+"F1.opExtrude","SWEPT_FACE",FACE,{"disambiguationData":[OSD([subQ1])]});Q24=makeQuery(id+"F10.opFillet","BLEND_EDGE",EDGE,{"blendedFrom":[makeQuery(id+"F9.opChamfer","BLEND_EDGE",EDGE,{"blendedFrom":[makeQuery(id+"F1.opExtrude","SWEPT_EDGE",EDGE,{"disambiguationData":[OSD([subQ1,subQ0])]}),subQ3],"blendedInto":[subQ3]}),makeQuery(id+"F6.boolean.opBoolean","SPLIT",FACE,{"disambiguationData":[TD([subQ2,subQ3,makeQuery(id+"F1.opExtrude","SWEPT_FACE",FACE,{"disambiguationData":[OSD([subQ0])]}),makeQuery(id+"F6.opExtrude","SWEPT_FACE",FACE,{"disambiguationData":[OSD([sQuery(id+"F0.wireOp",EDGE,"E6")])]})])],"derivedFrom":subQ2})],"blendedInto":[makeQuery(id+"F6.boolean.opBoolean","SPLIT",FACE,{"disambiguationData":[TD([subQ2,subQ3,makeQuery(id+"F1.opExtrude","SWEPT_FACE",FACE,{"disambiguationData":[OSD([subQ0])]}),makeQuery(id+"F6.opExtrude","SWEPT_FACE",FACE,{"disambiguationData":[OSD([sQuery(id+"F0.wireOp",EDGE,"E6")])]})])],"derivedFrom":subQ2})]});}
            var Q25;
            Q25=makeQuery(id+"F6.opExtrude","CAP_EDGE",EDGE,{"disambiguationData":[OSD([sQuery(id+"F0.wireOp",EDGE,"E6")])],"isStart":false});
            fillet(context, id + "F12", {"entities" : qUnion([Q0, Q1, Q2, Q3, Q4, Q5, Q6, Q7, Q8, Q9, Q10, Q11, Q12, Q13, Q14, Q15, Q16, Q17, Q18, Q19, Q20, Q21, Q22, Q23, Q24, Q25]), "radius" : 0.89 * mm, "tangentPropagation" : true, "allowEdgeOverflow" : false});
        }
    });
